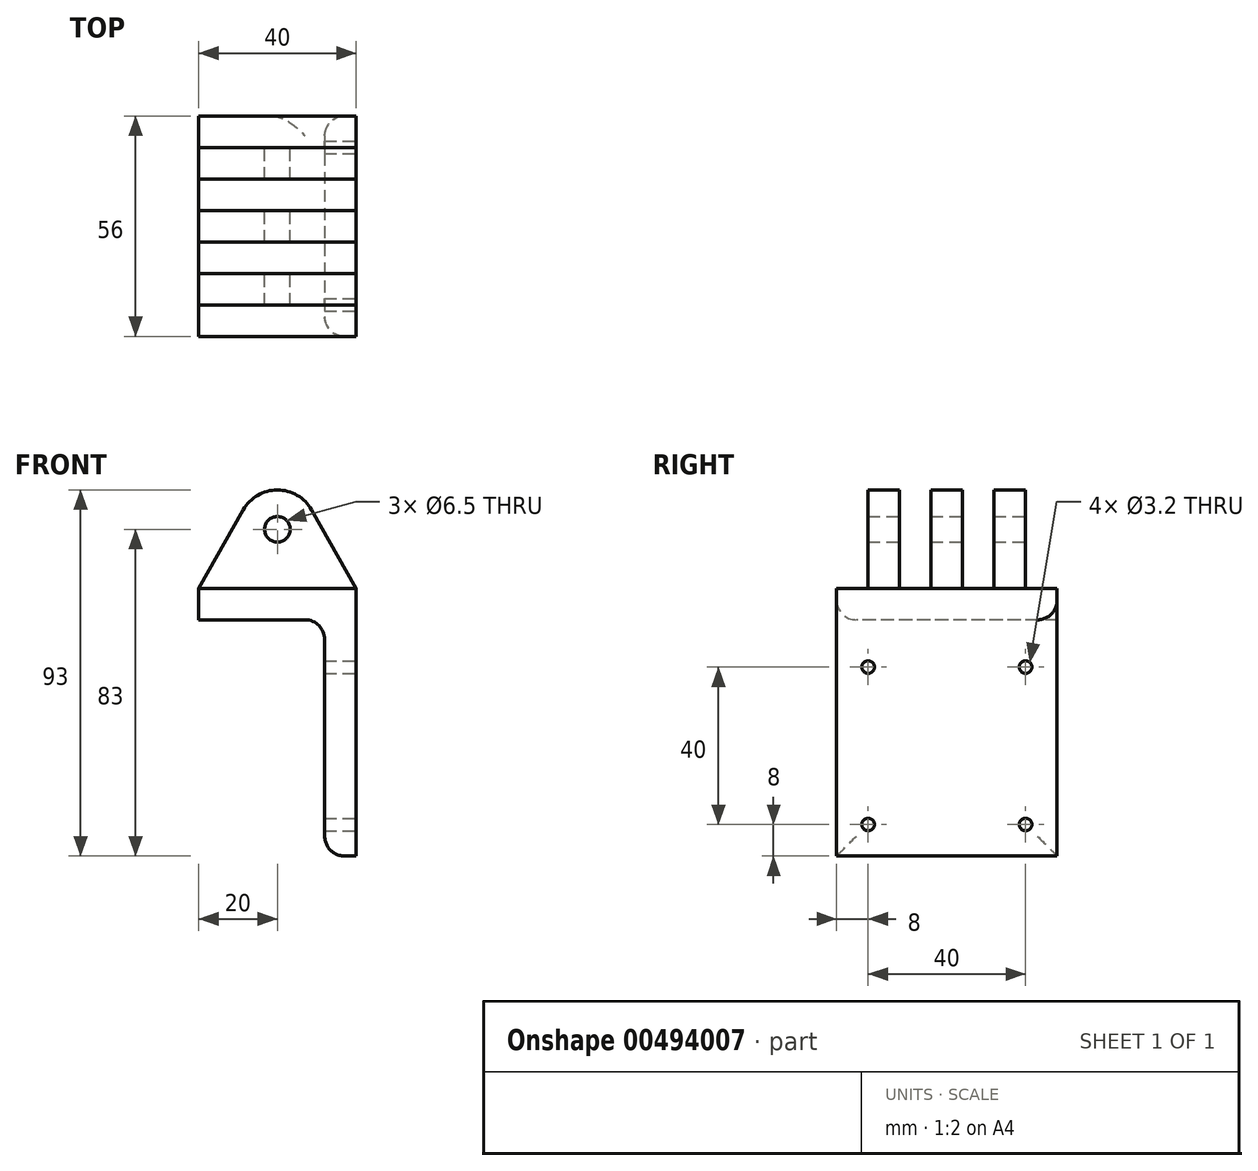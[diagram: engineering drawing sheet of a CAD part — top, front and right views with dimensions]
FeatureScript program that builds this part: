
annotation { "Feature Type Name" : "Feature", "Feature Type Description" : "" }
export const myFeature = defineFeature(function(context is Context, id is Id, definition is map)
    precondition{}
    {
        {
            var Q0;
            Q0=qCreatedBy(makeId("Front.planeOp"),FACE);
            var sketch = newSketch(context, id + "F0", { "sketchPlane" : qUnion([Q0])});
            skLineSegment(sketch, "E0.bottom", {"start": v(0, 0) * mm, "end": v(40, 0) * mm});
            skLineSegment(sketch, "E0.top", {"start": v(0, 25) * mm, "end": v(40, 25) * mm});
            skLineSegment(sketch, "E0.left", {"start": v(0, 0) * mm, "end": v(0, 25) * mm});
            skLineSegment(sketch, "E0.right", {"start": v(40, 0) * mm, "end": v(40, 25) * mm});
            skLineSegment(sketch, "E1", {"start": v(20, 0) * mm, "end": v(20, 15) * mm});
            skCircle(sketch, "E2", {"center": v(20, 15) * mm, "radius": 3.25 * mm});
            skCircle(sketch, "E3", {"center": v(20, 15) * mm, "radius": 10 * mm});
            skLineSegment(sketch, "E4", {"start": v(0, 0) * mm, "end": v(11.3, 19.93) * mm});
            skLineSegment(sketch, "E5", {"start": v(40, 0) * mm, "end": v(28.7, 19.93) * mm});
            skSolve(sketch);
        }
        {
            var Q0;
            Q0=makeQuery(id+"F0.imprint","IMPRINT",FACE,{"disambiguationData":[TD([[makeQuery(id+"F0.imprint","IMPRINT",EDGE,{"derivedFrom":sQuery(id+"F0.wireOp",EDGE,"E2")}),-1.0]])]});
            var Q1;
            {var subQ0=sQuery(id+"F0.wireOp",EDGE,"E4");Q1=makeQuery(id+"F0.imprint","IMPRINT",FACE,{"disambiguationData":[TD([[makeQuery(id+"F0.imprint","IMPRINT",EDGE,{"derivedFrom":subQ0}),-1.0]])]});}
            var Q2;
            {var subQ0=sQuery(id+"F0.wireOp",EDGE,"E5");Q2=makeQuery(id+"F0.imprint","IMPRINT",FACE,{"disambiguationData":[TD([[makeQuery(id+"F0.imprint","IMPRINT",EDGE,{"derivedFrom":subQ0}),1.0]])]});}
            extrude(context, id + "F1", {"entities" : qUnion([Q0, Q1, Q2]), "depth" : 40 * mm});
        }
        {
            var Q0;
            Q0=qCreatedBy(makeId("Right.planeOp"),FACE);
            var sketch = newSketch(context, id + "F2", { "sketchPlane" : qUnion([Q0])});
            skLineSegment(sketch, "E6.bottom", {"start": v(0, 0) * mm, "end": v(-40, 0) * mm});
            skLineSegment(sketch, "E6.top", {"start": v(0, 25) * mm, "end": v(-40, 25) * mm});
            skLineSegment(sketch, "E6.left", {"start": v(0, 0) * mm, "end": v(0, 25) * mm});
            skLineSegment(sketch, "E6.right", {"start": v(-40, 0) * mm, "end": v(-40, 25) * mm});
            skLineSegment(sketch, "E7", {"start": v(-8, 0) * mm, "end": v(-8, 25) * mm});
            skLineSegment(sketch, "E8", {"start": v(-16, 25) * mm, "end": v(-16, 0) * mm});
            skLineSegment(sketch, "E9", {"start": v(-24, 25) * mm, "end": v(-24, 0) * mm});
            skLineSegment(sketch, "E10", {"start": v(-32, 25) * mm, "end": v(-32, 0) * mm});
            skSolve(sketch);
        }
        {
            var Q0;
            {var subQ1=sQuery(id+"F2.wireOp",EDGE,"E9");Q0=makeQuery(id+"F2.imprint","IMPRINT",FACE,{"disambiguationData":[TD([[makeQuery(id+"F2.imprint","IMPRINT",EDGE,{"derivedFrom":subQ1}),-1.0]])]});}
            var Q1;
            {var subQ1=sQuery(id+"F2.wireOp",EDGE,"E7");Q1=makeQuery(id+"F2.imprint","IMPRINT",FACE,{"disambiguationData":[TD([[makeQuery(id+"F2.imprint","IMPRINT",EDGE,{"derivedFrom":subQ1}),1.0]])]});}
            extrude(context, id + "F3", {"entities" : qUnion([Q0, Q1]), "operationType" : NewBodyOperationType.REMOVE, "depth" : 40 * mm});
        }
        {
            var Q0;
            Q0=makeQuery(id+"F1.opExtrude","CAP_FACE",FACE,{"disambiguationData":[OSD([sQuery(id+"F0.wireOp",EDGE,"E0.bottom"),sQuery(id+"F0.wireOp",EDGE,"E2"),sQuery(id+"F0.wireOp",EDGE,"E3"),sQuery(id+"F0.wireOp",EDGE,"E4"),sQuery(id+"F0.wireOp",EDGE,"E5")])],"isStart":false});
            var sketch = newSketch(context, id + "F4", { "sketchPlane" : qUnion([Q0])});
            skLineSegment(sketch, "E11.bottom", {"start": v(0, 0) * mm, "end": v(40, 0) * mm});
            skLineSegment(sketch, "E11.top", {"start": v(0, -68) * mm, "end": v(40, -68) * mm});
            skLineSegment(sketch, "E11.left", {"start": v(0, 0) * mm, "end": v(0, -68) * mm});
            skLineSegment(sketch, "E11.right", {"start": v(40, 0) * mm, "end": v(40, -68) * mm});
            skLineSegment(sketch, "E12", {"start": v(0, -8) * mm, "end": v(32, -8) * mm});
            skLineSegment(sketch, "E13", {"start": v(32, -8) * mm, "end": v(32, -68) * mm});
            skSolve(sketch);
        }
        {
            var Q0;
            {var subQ1=sQuery(id+"F4.wireOp",EDGE,"E11.bottom");Q0=makeQuery(id+"F4.imprint","IMPRINT",FACE,{"disambiguationData":[TD([[makeQuery(id+"F4.imprint","IMPRINT",EDGE,{"derivedFrom":subQ1}),-1.0]])]});}
            var Q1;
            Q1=makeQuery(id+"F1.opExtrude","CAP_FACE",FACE,{"disambiguationData":[OSD([sQuery(id+"F0.wireOp",EDGE,"E0.bottom"),sQuery(id+"F0.wireOp",EDGE,"E2"),sQuery(id+"F0.wireOp",EDGE,"E3"),sQuery(id+"F0.wireOp",EDGE,"E4"),sQuery(id+"F0.wireOp",EDGE,"E5")])],"isStart":true});
            extrude(context, id + "F5", {"entities" : qUnion([Q0]), "oppositeDirection" : true, "endBoundEntityFace" : qUnion([Q1]), "depth" : 48 * mm, "hasSecondDirection" : true, "secondDirectionOppositeDirection" : false, "secondDirectionDepth" : 8 * mm});
        }
        {
            var Q0;
            Q0=makeQuery(id+"F5.opExtrude","CAP_EDGE",EDGE,{"disambiguationData":[OSD([sQuery(id+"F4.wireOp",EDGE,"E13")])],"isStart":true});
            var Q1;
            Q1=makeQuery(id+"F5.opExtrude","CAP_EDGE",EDGE,{"disambiguationData":[OSD([sQuery(id+"F4.wireOp",EDGE,"E12")])],"isStart":true});
            var Q2;
            Q2=makeQuery(id+"F5.opExtrude","SWEPT_EDGE",EDGE,{"disambiguationData":[OSD([sQuery(id+"F4.wireOp",EDGE,"E11.top"),sQuery(id+"F4.wireOp",EDGE,"E13")])]});
            var Q3;
            Q3=makeQuery(id+"F5.opExtrude","SWEPT_EDGE",EDGE,{"disambiguationData":[OSD([sQuery(id+"F4.wireOp",EDGE,"E12"),sQuery(id+"F4.wireOp",EDGE,"E13")])]});
            var Q4;
            Q4=makeQuery(id+"F5.opExtrude","CAP_EDGE",EDGE,{"disambiguationData":[OSD([sQuery(id+"F4.wireOp",EDGE,"E13")])],"isStart":false});
            fillet(context, id + "F6", {"entities" : qUnion([Q0, Q1, Q2, Q3, Q4]), "radius" : 5 * mm, "tangentPropagation" : true, "allowEdgeOverflow" : false});
        }
        {
            var Q0;
            Q0=makeQuery(id+"F5.opExtrude","SWEPT_FACE",FACE,{"disambiguationData":[OSD([sQuery(id+"F4.wireOp",EDGE,"E11.right")])]});
            var sketch = newSketch(context, id + "F7", { "sketchPlane" : qUnion([Q0])});
            skLineSegment(sketch, "E14", {"start": v(-20, -68) * mm, "end": v(-20, -40) * mm});
            skLineSegment(sketch, "E15.bottom", {"start": v(0, -20) * mm, "end": v(-40, -20) * mm});
            skLineSegment(sketch, "E15.top", {"start": v(0, -60) * mm, "end": v(-40, -60) * mm});
            skLineSegment(sketch, "E15.left", {"start": v(0, -20) * mm, "end": v(0, -60) * mm});
            skLineSegment(sketch, "E15.right", {"start": v(-40, -20) * mm, "end": v(-40, -60) * mm});
            skPoint(sketch, "E15.middle", {"position": v(-20, -40) * mm});
            skCircle(sketch, "E16", {"center": v(-40, -20) * mm, "radius": 1.6 * mm});
            skCircle(sketch, "E17", {"center": v(0, -20) * mm, "radius": 1.6 * mm});
            skCircle(sketch, "E18", {"center": v(-40, -60) * mm, "radius": 1.6 * mm});
            skCircle(sketch, "E19", {"center": v(0, -60) * mm, "radius": 1.6 * mm});
            skSolve(sketch);
        }
        {
            var Q0;
            {var subQ0=sQuery(id+"F7.wireOp",EDGE,"E15.left");var subQ1=sQuery(id+"F7.wireOp",EDGE,"E15.bottom");var subQ2=makeQuery(id+"F7.imprint","INTERSECT",VERTEX,{"derivedFrom":[subQ1,subQ0]});Q0=makeQuery(id+"F7.imprint","IMPRINT",FACE,{"disambiguationData":[TD([[makeQuery(id+"F7.imprint","IMPRINT",EDGE,{"disambiguationData":[TD([[subQ2,-1.0]])],"derivedFrom":subQ1}),1.0]])]});}
            var Q1;
            {var subQ0=sQuery(id+"F7.wireOp",EDGE,"E15.left");var subQ1=sQuery(id+"F7.wireOp",EDGE,"E15.bottom");var subQ2=makeQuery(id+"F7.imprint","INTERSECT",VERTEX,{"derivedFrom":[subQ1,subQ0]});Q1=makeQuery(id+"F7.imprint","IMPRINT",FACE,{"disambiguationData":[TD([[makeQuery(id+"F7.imprint","IMPRINT",EDGE,{"disambiguationData":[TD([[subQ2,-1.0]])],"derivedFrom":subQ1}),-1.0]])]});}
            var Q2;
            {var subQ0=sQuery(id+"F7.wireOp",EDGE,"E15.right");var subQ1=sQuery(id+"F7.wireOp",EDGE,"E15.bottom");var subQ2=makeQuery(id+"F7.imprint","INTERSECT",VERTEX,{"derivedFrom":[subQ1,subQ0]});Q2=makeQuery(id+"F7.imprint","IMPRINT",FACE,{"disambiguationData":[TD([[makeQuery(id+"F7.imprint","IMPRINT",EDGE,{"disambiguationData":[TD([[subQ2,1.0]])],"derivedFrom":subQ1}),-1.0]])]});}
            var Q3;
            {var subQ0=sQuery(id+"F7.wireOp",EDGE,"E15.right");var subQ1=sQuery(id+"F7.wireOp",EDGE,"E15.bottom");var subQ2=makeQuery(id+"F7.imprint","INTERSECT",VERTEX,{"derivedFrom":[subQ1,subQ0]});Q3=makeQuery(id+"F7.imprint","IMPRINT",FACE,{"disambiguationData":[TD([[makeQuery(id+"F7.imprint","IMPRINT",EDGE,{"disambiguationData":[TD([[subQ2,1.0]])],"derivedFrom":subQ1}),1.0]])]});}
            var Q4;
            {var subQ0=sQuery(id+"F7.wireOp",EDGE,"E15.left");var subQ1=sQuery(id+"F7.wireOp",EDGE,"E15.top");var subQ2=makeQuery(id+"F7.imprint","INTERSECT",VERTEX,{"derivedFrom":[subQ1,subQ0]});Q4=makeQuery(id+"F7.imprint","IMPRINT",FACE,{"disambiguationData":[TD([[makeQuery(id+"F7.imprint","IMPRINT",EDGE,{"disambiguationData":[TD([[subQ2,-1.0]])],"derivedFrom":subQ1}),-1.0]])]});}
            var Q5;
            {var subQ0=sQuery(id+"F7.wireOp",EDGE,"E15.left");var subQ1=sQuery(id+"F7.wireOp",EDGE,"E15.top");var subQ2=makeQuery(id+"F7.imprint","INTERSECT",VERTEX,{"derivedFrom":[subQ1,subQ0]});Q5=makeQuery(id+"F7.imprint","IMPRINT",FACE,{"disambiguationData":[TD([[makeQuery(id+"F7.imprint","IMPRINT",EDGE,{"disambiguationData":[TD([[subQ2,-1.0]])],"derivedFrom":subQ1}),1.0]])]});}
            var Q6;
            {var subQ0=sQuery(id+"F7.wireOp",EDGE,"E15.right");var subQ1=sQuery(id+"F7.wireOp",EDGE,"E15.top");var subQ2=makeQuery(id+"F7.imprint","INTERSECT",VERTEX,{"derivedFrom":[subQ1,subQ0]});Q6=makeQuery(id+"F7.imprint","IMPRINT",FACE,{"disambiguationData":[TD([[makeQuery(id+"F7.imprint","IMPRINT",EDGE,{"disambiguationData":[TD([[subQ2,1.0]])],"derivedFrom":subQ1}),-1.0]])]});}
            var Q7;
            {var subQ0=sQuery(id+"F7.wireOp",EDGE,"E15.right");var subQ1=sQuery(id+"F7.wireOp",EDGE,"E15.top");var subQ2=makeQuery(id+"F7.imprint","INTERSECT",VERTEX,{"derivedFrom":[subQ1,subQ0]});Q7=makeQuery(id+"F7.imprint","IMPRINT",FACE,{"disambiguationData":[TD([[makeQuery(id+"F7.imprint","IMPRINT",EDGE,{"disambiguationData":[TD([[subQ2,1.0]])],"derivedFrom":subQ1}),1.0]])]});}
            extrude(context, id + "F8", {"entities" : qUnion([Q0, Q1, Q2, Q3, Q4, Q5, Q6, Q7]), "operationType" : NewBodyOperationType.REMOVE, "oppositeDirection" : true, "depth" : 25 * mm});
        }
    });
